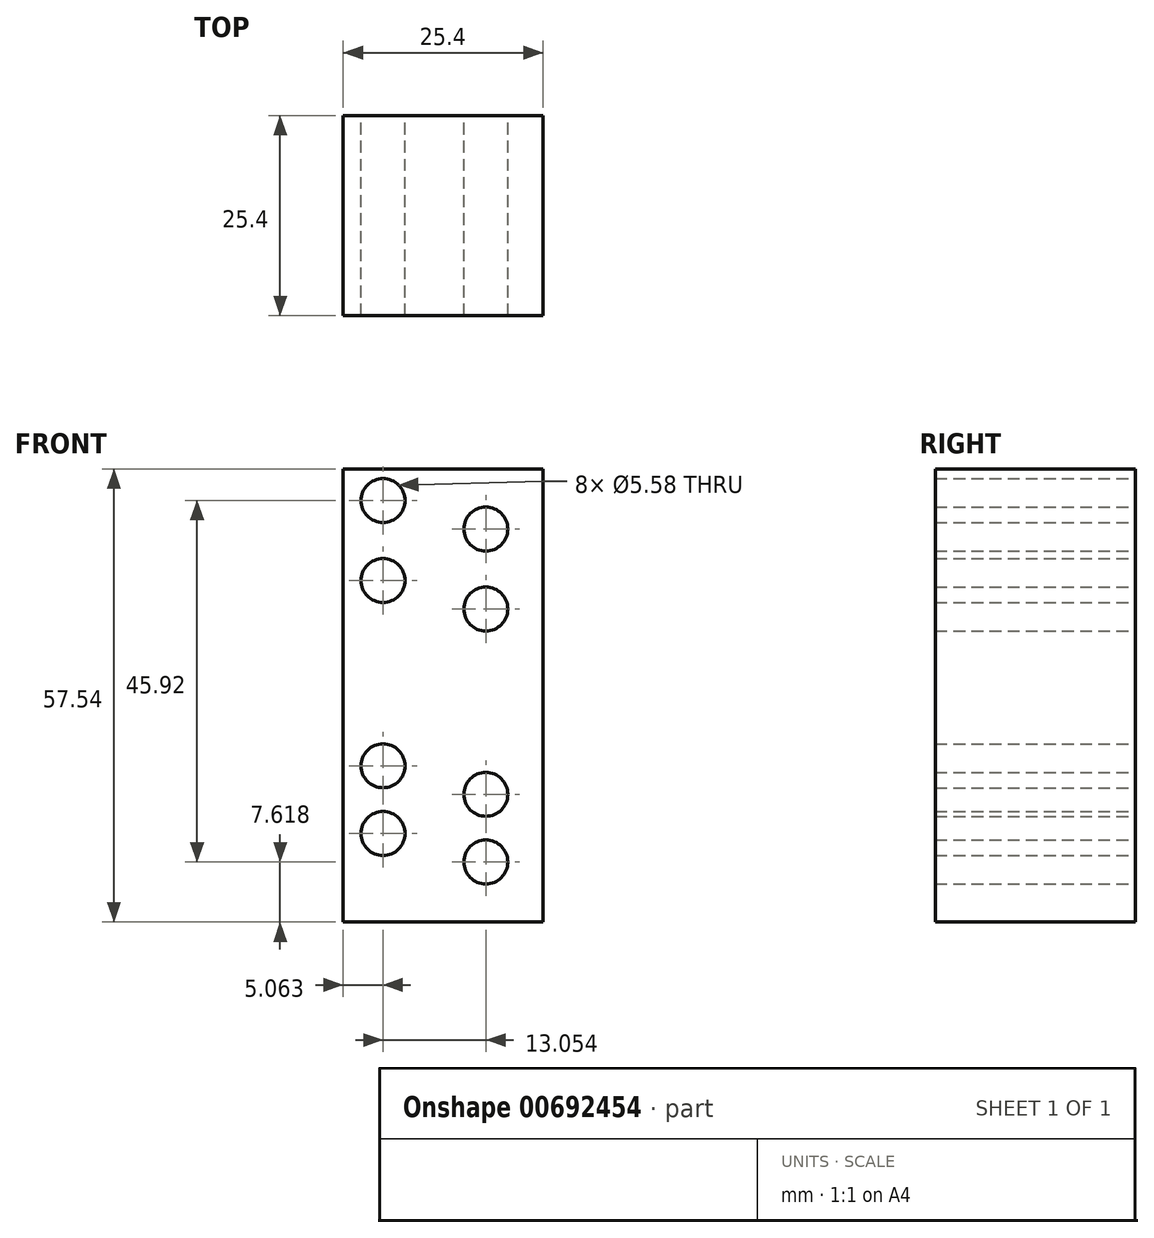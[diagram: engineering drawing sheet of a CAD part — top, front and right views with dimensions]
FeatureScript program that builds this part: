
annotation { "Feature Type Name" : "Feature", "Feature Type Description" : "" }
export const myFeature = defineFeature(function(context is Context, id is Id, definition is map)
    precondition{}
    {
        {
            var Q0;
            Q0=qCreatedBy(makeId("Front.planeOp"),FACE);
            var sketch = newSketch(context, id + "F0", { "sketchPlane" : qUnion([Q0])});
            skLineSegment(sketch, "E0.bottom", {"start": v(-64.54, 29.8) * mm, "end": v(-39.14, 29.8) * mm});
            skLineSegment(sketch, "E0.top", {"start": v(-64.54, -27.74) * mm, "end": v(-39.14, -27.74) * mm});
            skLineSegment(sketch, "E0.left", {"start": v(-64.54, 29.8) * mm, "end": v(-64.54, -27.74) * mm});
            skLineSegment(sketch, "E0.right", {"start": v(-39.14, 29.8) * mm, "end": v(-39.14, -27.74) * mm});
            skCircle(sketch, "E1", {"center": v(-46.42, 22.18) * mm, "radius": 2.8 * mm});
            skCircle(sketch, "E2", {"center": v(-46.42, 12.02) * mm, "radius": 2.8 * mm});
            skPoint(sketch, "E3", {"position": v(-51.84, 29.8) * mm});
            skPoint(sketch, "E4", {"position": v(-51.84, -27.74) * mm});
            skCircle(sketch, "E5", {"center": v(-46.42, -11.52) * mm, "radius": 2.8 * mm});
            skCircle(sketch, "E6", {"center": v(-46.42, -20.12) * mm, "radius": 2.8 * mm});
            skCircle(sketch, "E7", {"center": v(-59.48, 25.8) * mm, "radius": 2.8 * mm});
            skCircle(sketch, "E8", {"center": v(-59.48, 15.64) * mm, "radius": 2.8 * mm});
            skCircle(sketch, "E9", {"center": v(-59.48, -7.9) * mm, "radius": 2.8 * mm});
            skCircle(sketch, "E10", {"center": v(-59.48, -16.5) * mm, "radius": 2.8 * mm});
            skSolve(sketch);
        }
        {
            var Q0;
            Q0 = qSketchRegion(id + "F0", true);
            extrude(context, id + "F1", {"entities" : qUnion([Q0]), "depth" : 25.4 * mm, "offsetDistance" : 25.4 * mm});
        }
    });
